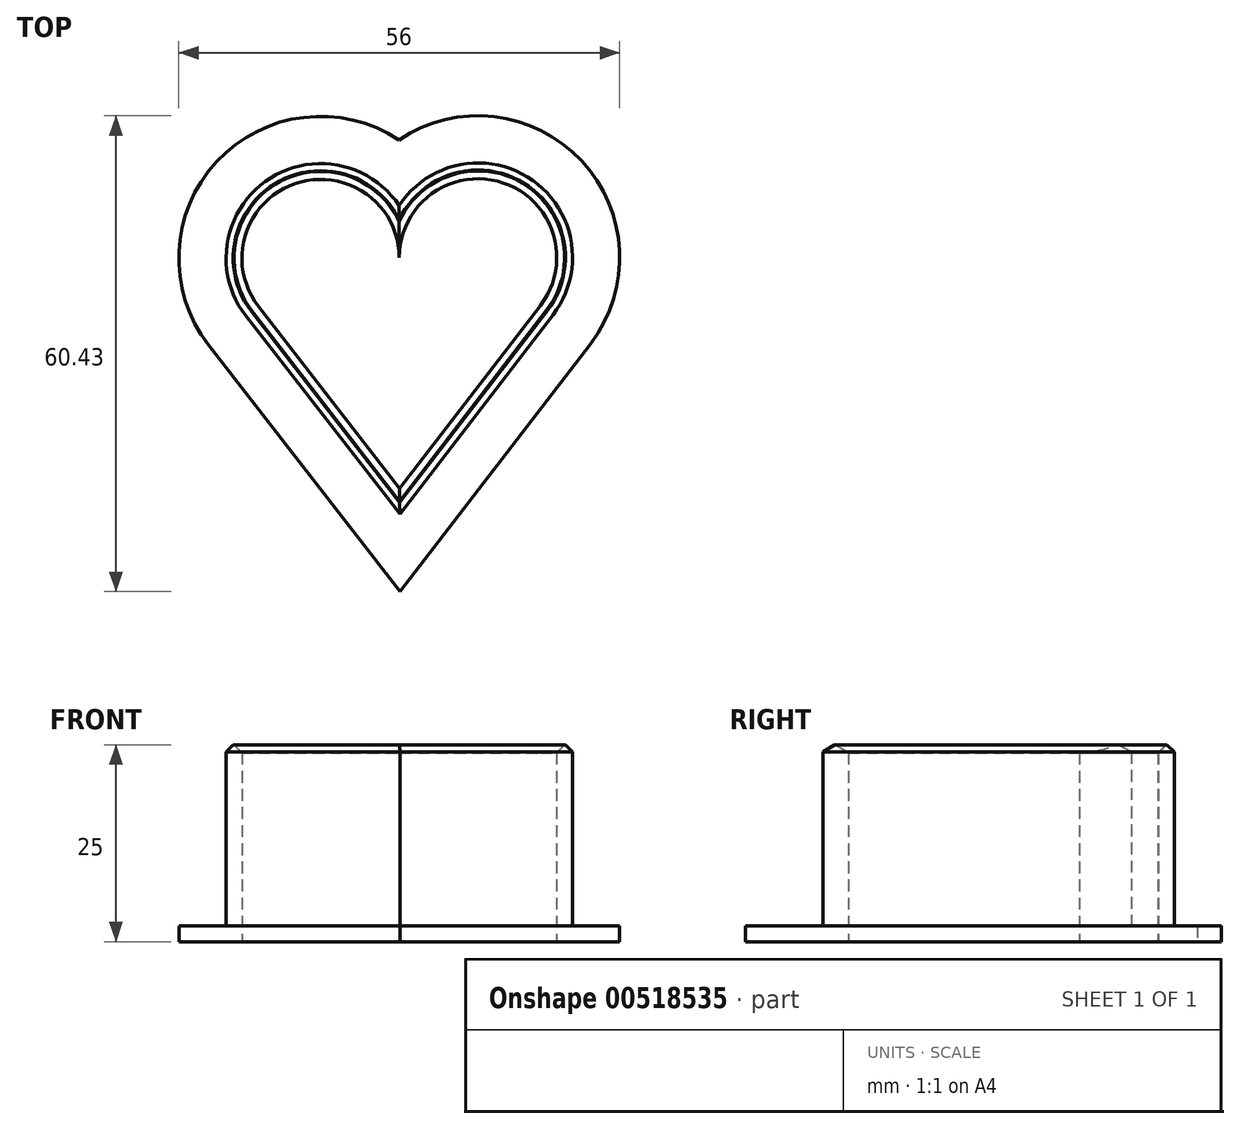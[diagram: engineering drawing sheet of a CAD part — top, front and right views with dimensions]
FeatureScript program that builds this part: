
annotation { "Feature Type Name" : "Feature", "Feature Type Description" : "" }
export const myFeature = defineFeature(function(context is Context, id is Id, definition is map)
    precondition{}
    {
        {
            var Q0;
            Q0=qCreatedBy(makeId("Top.planeOp"),FACE);
            var sketch = newSketch(context, id + "F0", { "sketchPlane" : qUnion([Q0])});
            skCircle(sketch, "E0", {"center": v(0, 0) * mm, "radius": 7.5 * mm, "construction": true});
            skLineSegment(sketch, "E1", {"start": v(-0.05, 14.05) * mm, "end": v(0, -14.95) * mm, "construction": true});
            skLineSegment(sketch, "E2", {"start": v(0, -14.95) * mm, "end": v(17.87, 8.3) * mm});
            skLineSegment(sketch, "E3", {"start": v(0, -14.95) * mm, "end": v(-17.96, 8.2) * mm});
            skArc(sketch, "E4", {"start": v(-0.06, 14.36) * mm, "mid": v(-13.32, 23.78) * mm, "end": v(-17.96, 8.2) * mm});
            skArc(sketch, "E5", {"start": v(-17.96, 8.2) * mm, "mid": v(-6.8, 4.87) * mm, "end": v(-0.06, 14.36) * mm, "construction": true});
            skArc(sketch, "E6", {"start": v(17.87, 8.3) * mm, "mid": v(13.14, 23.87) * mm, "end": v(-0.06, 14.36) * mm});
            skArc(sketch, "E7", {"start": v(-0.06, 14.36) * mm, "mid": v(6.74, 4.93) * mm, "end": v(17.87, 8.3) * mm, "construction": true});
            skArc(sketch, "E8.0", {"start": v(-0.08, 21) * mm, "mid": v(-17.08, 24.05) * mm, "end": v(-19.54, 6.96) * mm});
            skArc(sketch, "E8.1", {"start": v(19.46, 7.09) * mm, "mid": v(16.9, 24.18) * mm, "end": v(-0.08, 21) * mm});
            skLineSegment(sketch, "E8.2", {"start": v(0, -18.22) * mm, "end": v(19.46, 7.09) * mm});
            skLineSegment(sketch, "E8.3", {"start": v(0, -18.22) * mm, "end": v(-19.54, 6.96) * mm});
            skArc(sketch, "E9.0", {"start": v(24.21, 3.43) * mm, "mid": v(23.06, 26.73) * mm, "end": v(-0.12, 29.33) * mm});
            skLineSegment(sketch, "E9.1", {"start": v(0.03, -28.03) * mm, "end": v(24.21, 3.43) * mm});
            skLineSegment(sketch, "E9.2", {"start": v(0.03, -28.03) * mm, "end": v(-24.28, 3.29) * mm});
            skArc(sketch, "E9.3", {"start": v(-0.12, 29.33) * mm, "mid": v(-23.25, 26.56) * mm, "end": v(-24.28, 3.29) * mm});
            skSolve(sketch);
        }
        {
            var Q0;
            Q0=makeQuery(id+"F0.imprint","IMPRINT",FACE,{"disambiguationData":[TD([[makeQuery(id+"F0.imprint","IMPRINT",EDGE,{"derivedFrom":sQuery(id+"F0.wireOp",EDGE,"E2")}),-1.0]])]});
            extrude(context, id + "F1", {"entities" : qUnion([Q0]), "depth" : 25 * mm, "offsetDistance" : 25 * mm});
        }
        {
            var Q0;
            Q0=makeQuery(id+"F1.opExtrude","CAP_EDGE",EDGE,{"disambiguationData":[OSD([sQuery(id+"F0.wireOp",EDGE,"E3")])],"isStart":false});
            var Q1;
            Q1=makeQuery(id+"F1.opExtrude","CAP_EDGE",EDGE,{"disambiguationData":[OSD([sQuery(id+"F0.wireOp",EDGE,"E2")])],"isStart":false});
            var Q2;
            Q2=makeQuery(id+"F1.opExtrude","CAP_EDGE",EDGE,{"disambiguationData":[OSD([sQuery(id+"F0.wireOp",EDGE,"E6")])],"isStart":false});
            var Q3;
            Q3=makeQuery(id+"F1.opExtrude","CAP_EDGE",EDGE,{"disambiguationData":[OSD([sQuery(id+"F0.wireOp",EDGE,"E4")])],"isStart":false});
            chamfer(context, id + "F2", {"entities" : qUnion([Q0, Q1, Q2, Q3]), "width" : 1 * mm, "tangentPropagation" : true});
        }
        {
            var Q0;
            Q0=makeQuery(id+"F1.opExtrude","CAP_EDGE",EDGE,{"disambiguationData":[OSD([sQuery(id+"F0.wireOp",EDGE,"E8.3")])],"isStart":false});
            var Q1;
            Q1=makeQuery(id+"F1.opExtrude","CAP_EDGE",EDGE,{"disambiguationData":[OSD([sQuery(id+"F0.wireOp",EDGE,"E8.0")])],"isStart":false});
            var Q2;
            Q2=makeQuery(id+"F1.opExtrude","CAP_EDGE",EDGE,{"disambiguationData":[OSD([sQuery(id+"F0.wireOp",EDGE,"E8.1")])],"isStart":false});
            var Q3;
            Q3=makeQuery(id+"F1.opExtrude","CAP_EDGE",EDGE,{"disambiguationData":[OSD([sQuery(id+"F0.wireOp",EDGE,"E8.2")])],"isStart":false});
            chamfer(context, id + "F3", {"entities" : qUnion([Q0, Q1, Q2, Q3]), "width" : .9 * mm, "tangentPropagation" : true});
        }
        {
            var Q0;
            Q0=makeQuery(id+"F0.imprint","IMPRINT",FACE,{"disambiguationData":[TD([[makeQuery(id+"F0.imprint","IMPRINT",EDGE,{"derivedFrom":sQuery(id+"F0.wireOp",EDGE,"E8.0")}),-1.0]])]});
            extrude(context, id + "F4", {"entities" : qUnion([Q0]), "operationType" : NewBodyOperationType.ADD, "depth" : 2 * mm, "offsetDistance" : 25 * mm});
        }
    });
